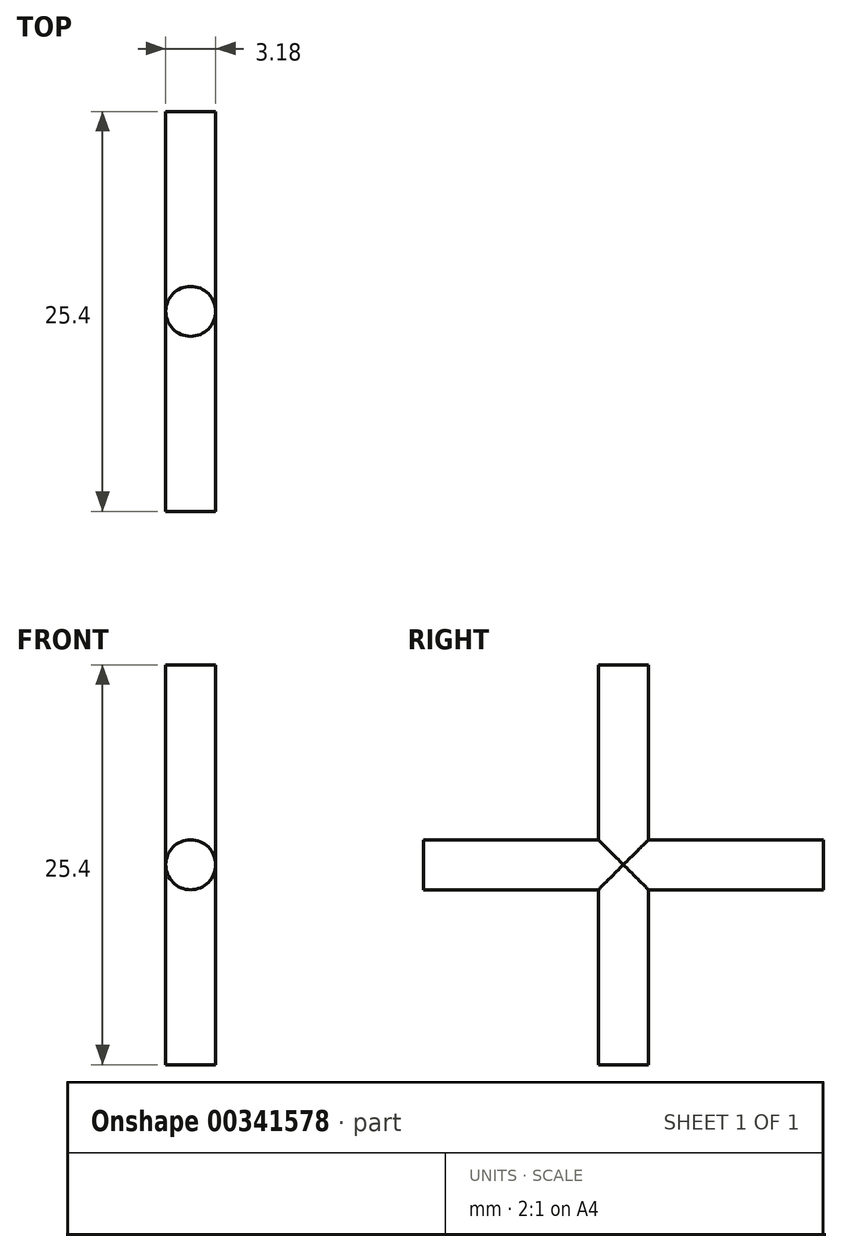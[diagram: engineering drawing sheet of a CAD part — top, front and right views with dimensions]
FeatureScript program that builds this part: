
annotation { "Feature Type Name" : "Feature", "Feature Type Description" : "" }
export const myFeature = defineFeature(function(context is Context, id is Id, definition is map)
    precondition{}
    {
        {
            var Q0;
            Q0=qCreatedBy(makeId("Top.planeOp"),FACE);
            var sketch = newSketch(context, id + "F0", { "sketchPlane" : qUnion([Q0])});
            skCircle(sketch, "E0", {"center": v(0, 0) * mm, "radius": 1.59 * mm});
            skSolve(sketch);
        }
        {
            var Q0;
            Q0 = qSketchRegion(id + "F0", true);
            extrude(context, id + "F1", {"entities" : qUnion([Q0]), "depth" : 25.4 * mm});
        }
        {
            var Q0;
            Q0=qCreatedBy(makeId("Front.planeOp"),FACE);
            var sketch = newSketch(context, id + "F2", { "sketchPlane" : qUnion([Q0])});
            skCircle(sketch, "E1", {"center": v(0, 12.7) * mm, "radius": 1.59 * mm});
            skSolve(sketch);
        }
        {
            var Q0;
            Q0 = qSketchRegion(id + "F2", true);
            extrude(context, id + "F3", {"entities" : qUnion([Q0]), "operationType" : NewBodyOperationType.ADD, "endBound" : BoundingType.SYMMETRIC, "depth" : 25.4 * mm});
        }
    });
